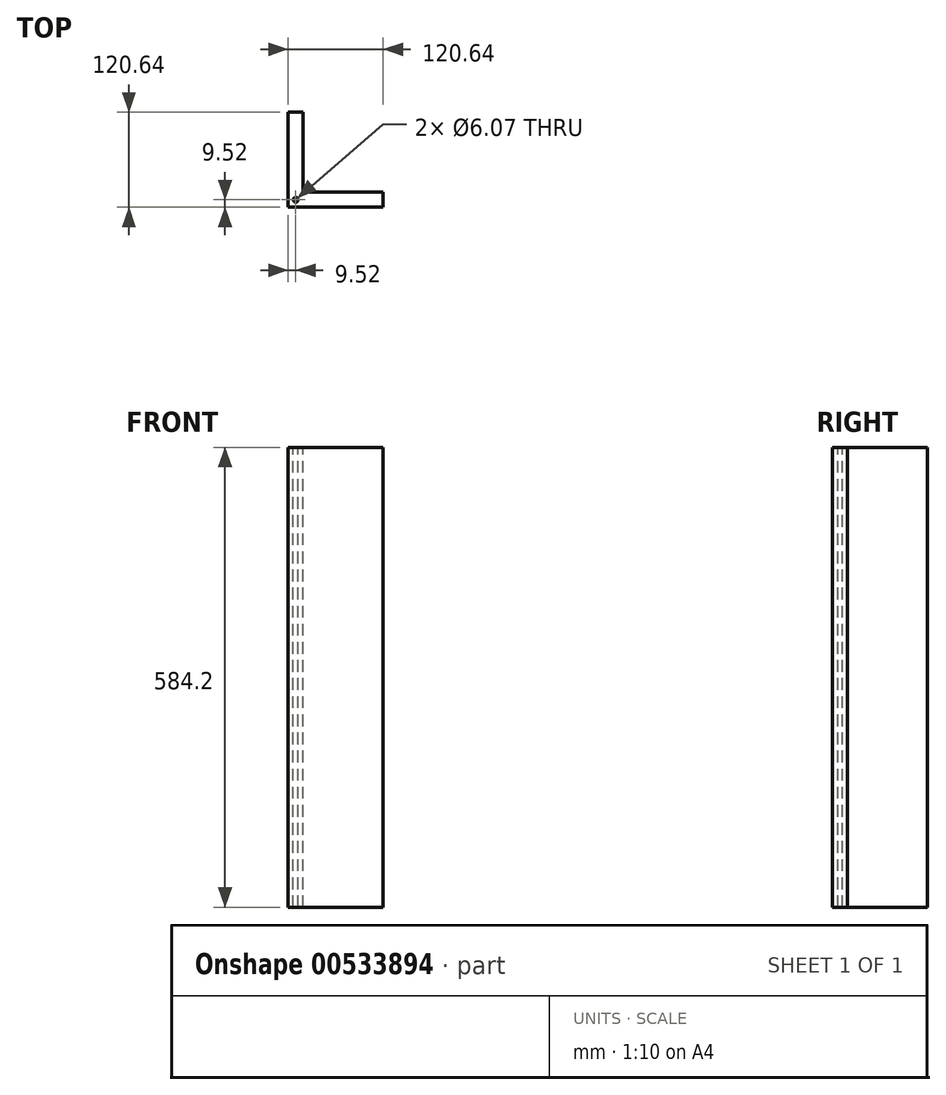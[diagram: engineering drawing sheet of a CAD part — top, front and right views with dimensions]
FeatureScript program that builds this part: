
annotation { "Feature Type Name" : "Feature", "Feature Type Description" : "" }
export const myFeature = defineFeature(function(context is Context, id is Id, definition is map)
    precondition{}
    {
        {
            var Q0;
            Q0=qCreatedBy(makeId("Top.planeOp"),FACE);
            var sketch = newSketch(context, id + "F0", { "sketchPlane" : qUnion([Q0])});
            skLineSegment(sketch, "E0.bottom", {"start": v(-60.32, -60.33) * mm, "end": v(60.33, -60.33) * mm});
            skLineSegment(sketch, "E0.top", {"start": v(-60.33, 60.33) * mm, "end": v(-41.27, 60.33) * mm});
            skLineSegment(sketch, "E0.left", {"start": v(-60.32, -60.33) * mm, "end": v(-60.33, 60.33) * mm});
            skLineSegment(sketch, "E0.right", {"start": v(60.33, -60.33) * mm, "end": v(60.33, -41.28) * mm});
            skPoint(sketch, "E0.middle", {"position": v(0, 0) * mm});
            skLineSegment(sketch, "E1", {"start": v(-41.27, 60.33) * mm, "end": v(-41.27, -41.28) * mm});
            skLineSegment(sketch, "E2", {"start": v(-41.27, -41.28) * mm, "end": v(60.33, -41.28) * mm});
            skPoint(sketch, "E3.orphan", {"position": v(60.32, 60.33) * mm});
            skSolve(sketch);
        }
        {
            var Q0;
            Q0=makeQuery(id+"F0.imprint","IMPRINT",FACE,{"disambiguationData":[TD([[makeQuery(id+"F0.imprint","IMPRINT",EDGE,{"derivedFrom":sQuery(id+"F0.wireOp",EDGE,"E0.bottom")}),1.0]])]});
            extrude(context, id + "F1", {"entities" : qUnion([Q0]), "endBound" : BoundingType.SYMMETRIC, "oppositeDirection" : true, "depth" : 584.2 * mm, "offsetDistance" : 25.4 * mm});
        }
        {
            var Q0;
            Q0=makeQuery(id+"F1.opExtrude","CAP_FACE",FACE,{"disambiguationData":[OSD([sQuery(id+"F0.wireOp",EDGE,"E0.bottom"),sQuery(id+"F0.wireOp",EDGE,"E0.left"),sQuery(id+"F0.wireOp",EDGE,"E0.top"),sQuery(id+"F0.wireOp",EDGE,"E0.right"),sQuery(id+"F0.wireOp",EDGE,"E1"),sQuery(id+"F0.wireOp",EDGE,"E2")])],"isStart":true});
            var sketch = newSketch(context, id + "F2", { "sketchPlane" : qUnion([Q0])});
            skLineSegment(sketch, "E4", {"start": v(-41.27, -41.28) * mm, "end": v(-60.32, -60.33) * mm});
            skCircle(sketch, "E5", {"center": v(-50.8, -50.8) * mm, "radius": 3.03 * mm});
            skSolve(sketch);
        }
        {
            var Q0;
            Q0 = qSketchRegion(id + "F2", true);
            extrude(context, id + "F3", {"entities" : qUnion([Q0]), "operationType" : NewBodyOperationType.REMOVE, "oppositeDirection" : true, "depth" : 611.63 * mm, "offsetDistance" : 25.4 * mm});
        }
    });
